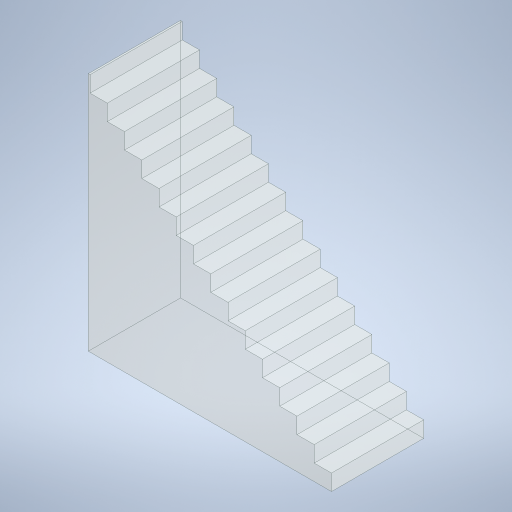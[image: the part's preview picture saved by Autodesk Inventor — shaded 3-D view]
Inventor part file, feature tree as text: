
AUTODESK INVENTOR PART (.ipt)
format: ipt  version: 2024.1 (Build 281209000, 209)  size: 302,080 bytes
history: native  units: in
note: dims shown in document units (in); Inventor stores cm internally (conversion verified against a paired STEP export)
features: extrude x1, sketch x1
ambient origin geometry x8: Origin, YZ Plane, XZ Plane, XY Plane, X Axis, Y Axis, Z Axis, Center Point
bodies: Solid1 (feature_tree)
feature tree (2):
  extrude  "Extrusion1"  Depth=104.25in
  sketch  "Sketch1"  dims[d4=40.0in d5=0.0in d21=104.25in d22=105.5in d23=0.75in]
